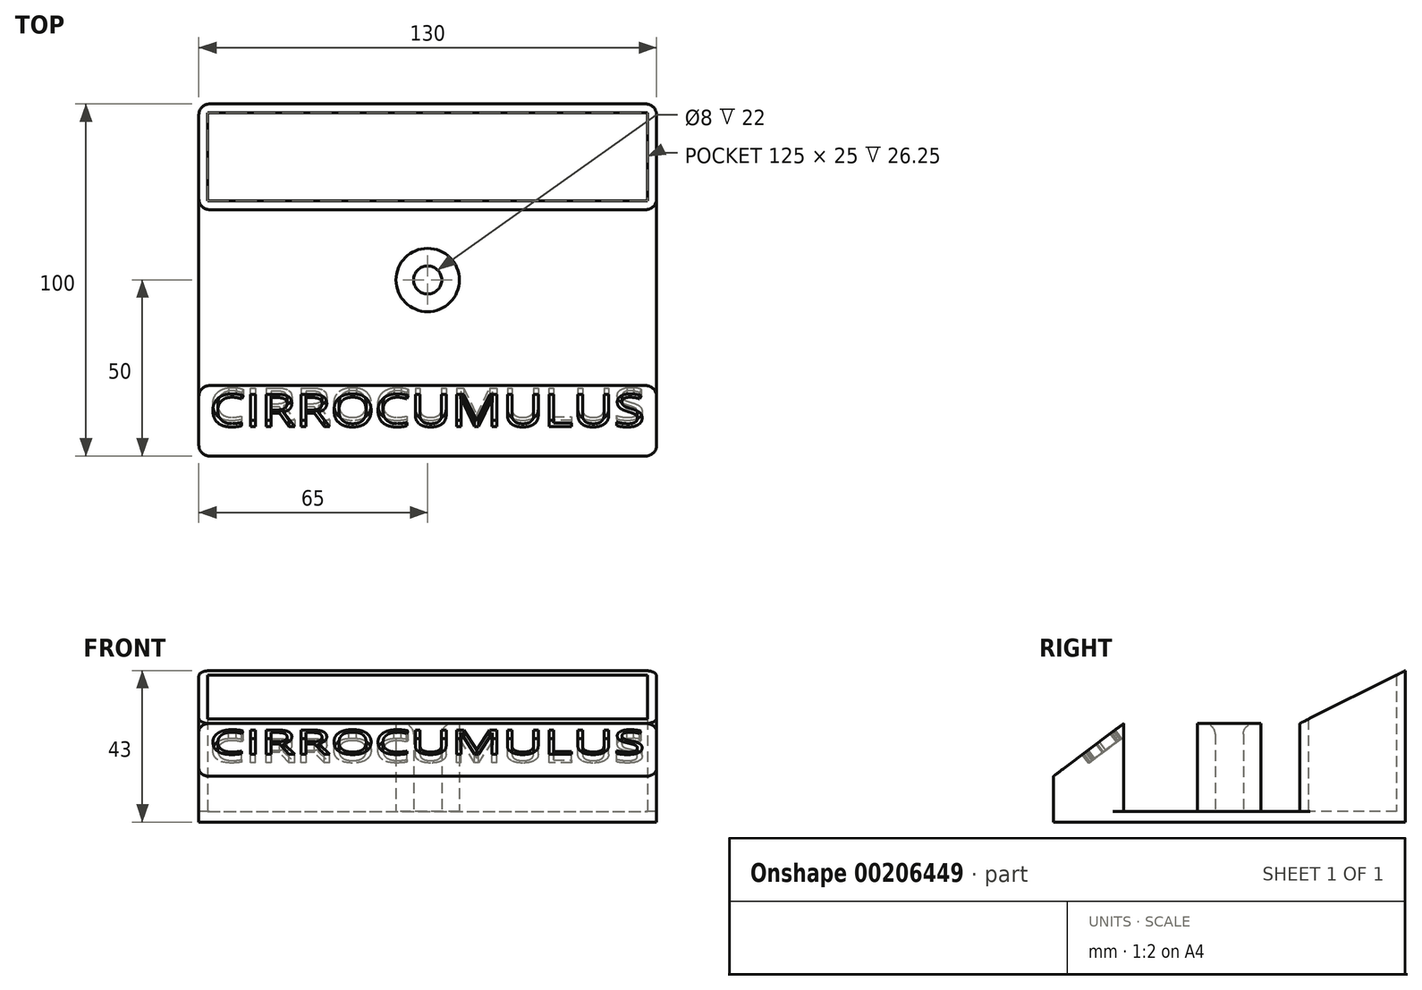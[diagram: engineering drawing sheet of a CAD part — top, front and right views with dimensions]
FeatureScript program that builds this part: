
annotation { "Feature Type Name" : "Feature", "Feature Type Description" : "" }
export const myFeature = defineFeature(function(context is Context, id is Id, definition is map)
    precondition{}
    {
        {
            var Q0;
            Q0=qCreatedBy(makeId("Top.planeOp"),FACE);
            var sketch = newSketch(context, id + "F0", { "sketchPlane" : qUnion([Q0])});
            skLineSegment(sketch, "E0.bottom", {"start": v(-65, 100) * mm, "end": v(65, 100) * mm});
            skLineSegment(sketch, "E0.top", {"start": v(-65, 0) * mm, "end": v(65, 0) * mm});
            skLineSegment(sketch, "E0.left", {"start": v(65, 100) * mm, "end": v(65, 0) * mm});
            skLineSegment(sketch, "E0.right", {"start": v(-65, 100) * mm, "end": v(-65, 0) * mm});
            skSolve(sketch);
        }
        {
            var Q0;
            Q0=makeQuery(id+"F0.imprint","IMPRINT",FACE,{"disambiguationData":[TD([[makeQuery(id+"F0.imprint","IMPRINT",EDGE,{"derivedFrom":sQuery(id+"F0.wireOp",EDGE,"E0.bottom")}),-1.0]])]});
            extrude(context, id + "F1", {"entities" : qUnion([Q0]), "depth" : 3 * mm});
        }
        {
            var Q0;
            Q0=makeQuery(id+"F1.opExtrude","CAP_FACE",FACE,{"disambiguationData":[OSD([sQuery(id+"F0.wireOp",EDGE,"E0.bottom"),sQuery(id+"F0.wireOp",EDGE,"E0.top"),sQuery(id+"F0.wireOp",EDGE,"E0.left"),sQuery(id+"F0.wireOp",EDGE,"E0.right")])],"isStart":false});
            var sketch = newSketch(context, id + "F2", { "sketchPlane" : qUnion([Q0])});
            skLineSegment(sketch, "E1", {"start": v(0, 0) * mm, "end": v(0, 100) * mm, "construction": true});
            skCircle(sketch, "E2", {"center": v(0, 50) * mm, "radius": 9 * mm});
            skCircle(sketch, "E3", {"center": v(0, 50) * mm, "radius": 4 * mm});
            skLineSegment(sketch, "E4.bottom", {"start": v(-65, 0) * mm, "end": v(65, 0) * mm});
            skLineSegment(sketch, "E4.top", {"start": v(-65, 20) * mm, "end": v(65, 20) * mm});
            skLineSegment(sketch, "E4.left", {"start": v(-65, 0) * mm, "end": v(-65, 20) * mm});
            skLineSegment(sketch, "E4.right", {"start": v(65, 0) * mm, "end": v(65, 20) * mm});
            skLineSegment(sketch, "E5.bottom", {"start": v(-65, 100) * mm, "end": v(65, 100) * mm});
            skLineSegment(sketch, "E5.top", {"start": v(-65, 70) * mm, "end": v(65, 70) * mm});
            skLineSegment(sketch, "E5.left", {"start": v(-65, 100) * mm, "end": v(-65, 70) * mm});
            skLineSegment(sketch, "E5.right", {"start": v(65, 100) * mm, "end": v(65, 70) * mm});
            skLineSegment(sketch, "E6.0", {"start": v(62.5, 97.5) * mm, "end": v(62.5, 72.5) * mm});
            skLineSegment(sketch, "E6.1", {"start": v(-62.5, 97.5) * mm, "end": v(62.5, 97.5) * mm});
            skLineSegment(sketch, "E6.2", {"start": v(-62.5, 97.5) * mm, "end": v(-62.5, 72.5) * mm});
            skLineSegment(sketch, "E6.3", {"start": v(-62.5, 72.5) * mm, "end": v(62.5, 72.5) * mm});
            skSolve(sketch);
        }
        {
            var Q0;
            Q0=makeQuery(id+"F2.imprint","IMPRINT",FACE,{"disambiguationData":[TD([[makeQuery(id+"F2.imprint","IMPRINT",EDGE,{"derivedFrom":sQuery(id+"F2.wireOp",EDGE,"E5.bottom")}),-1.0]])]});
            extrude(context, id + "F3", {"entities" : qUnion([Q0]), "operationType" : NewBodyOperationType.ADD, "depth" : 40 * mm});
        }
        {
            var Q0;
            Q0=makeQuery(id+"F2.imprint","IMPRINT",FACE,{"disambiguationData":[TD([[makeQuery(id+"F2.imprint","IMPRINT",EDGE,{"derivedFrom":sQuery(id+"F2.wireOp",EDGE,"E2")}),1.0]])]});
            var Q1;
            Q1=makeQuery(id+"F2.imprint","IMPRINT",FACE,{"disambiguationData":[TD([[makeQuery(id+"F2.imprint","IMPRINT",EDGE,{"derivedFrom":sQuery(id+"F2.wireOp",EDGE,"E4.bottom")}),1.0]])]});
            extrude(context, id + "F4", {"entities" : qUnion([Q0, Q1]), "operationType" : NewBodyOperationType.ADD, "depth" : 25 * mm});
        }
        {
            var Q0;
            Q0=makeQuery(id+"F4.opExtrude","CAP_EDGE",EDGE,{"disambiguationData":[OSD([sQuery(id+"F2.wireOp",EDGE,"E4.bottom")])],"isStart":false});
            chamfer(context, id + "F5", {"entities" : qUnion([Q0]), "chamferType" : ChamferType.TWO_OFFSETS, "width1" : 20 * mm, "oppositeDirection" : false, "width2" : 15 * mm, "tangentPropagation" : true});
        }
        {
            var Q0;
            Q0=makeQuery(id+"F3.opExtrude","CAP_EDGE",EDGE,{"disambiguationData":[OSD([sQuery(id+"F2.wireOp",EDGE,"E5.top")])],"isStart":false});
            chamfer(context, id + "F6", {"entities" : qUnion([Q0]), "chamferType" : ChamferType.TWO_OFFSETS, "width1" : 30 * mm, "oppositeDirection" : false, "width2" : 15 * mm, "tangentPropagation" : true});
        }
        {
            var Q0;
            Q0=makeQuery(id+"F3.boolean.opBoolean","MERGE",EDGE,{"derivedFrom":[makeQuery(id+"F1.opExtrude","SWEPT_EDGE",EDGE,{"disambiguationData":[OSD([sQuery(id+"F0.wireOp",EDGE,"E0.bottom"),sQuery(id+"F0.wireOp",EDGE,"E0.right")])]}),makeQuery(id+"F3.opExtrude","SWEPT_EDGE",EDGE,{"disambiguationData":[OSD([sQuery(id+"F2.wireOp",EDGE,"E5.bottom"),sQuery(id+"F2.wireOp",EDGE,"E5.left")])]})]});
            var Q1;
            Q1=makeQuery(id+"F3.opExtrude","SWEPT_EDGE",EDGE,{"disambiguationData":[OSD([sQuery(id+"F0.wireOp",EDGE,"E0.right"),sQuery(id+"F2.wireOp",EDGE,"E5.top"),sQuery(id+"F2.wireOp",EDGE,"E5.left")])]});
            var Q2;
            Q2=makeQuery(id+"F3.opExtrude","SWEPT_EDGE",EDGE,{"disambiguationData":[OSD([sQuery(id+"F0.wireOp",EDGE,"E0.left"),sQuery(id+"F2.wireOp",EDGE,"E5.top"),sQuery(id+"F2.wireOp",EDGE,"E5.right")])]});
            var Q3;
            Q3=makeQuery(id+"F4.boolean.opBoolean","MERGE",EDGE,{"derivedFrom":[makeQuery(id+"F1.opExtrude","SWEPT_EDGE",EDGE,{"disambiguationData":[OSD([sQuery(id+"F0.wireOp",EDGE,"E0.top"),sQuery(id+"F0.wireOp",EDGE,"E0.right")])]}),makeQuery(id+"F4.opExtrude","SWEPT_EDGE",EDGE,{"disambiguationData":[OSD([sQuery(id+"F2.wireOp",EDGE,"E4.bottom"),sQuery(id+"F2.wireOp",EDGE,"E4.left")])]})]});
            var Q4;
            Q4=makeQuery(id+"F3.boolean.opBoolean","MERGE",EDGE,{"derivedFrom":[makeQuery(id+"F1.opExtrude","SWEPT_EDGE",EDGE,{"disambiguationData":[OSD([sQuery(id+"F0.wireOp",EDGE,"E0.bottom"),sQuery(id+"F0.wireOp",EDGE,"E0.left")])]}),makeQuery(id+"F3.opExtrude","SWEPT_EDGE",EDGE,{"disambiguationData":[OSD([sQuery(id+"F2.wireOp",EDGE,"E5.bottom"),sQuery(id+"F2.wireOp",EDGE,"E5.right")])]})]});
            var Q5;
            Q5=makeQuery(id+"F4.boolean.opBoolean","MERGE",EDGE,{"derivedFrom":[makeQuery(id+"F1.opExtrude","SWEPT_EDGE",EDGE,{"disambiguationData":[OSD([sQuery(id+"F0.wireOp",EDGE,"E0.top"),sQuery(id+"F0.wireOp",EDGE,"E0.left")])]}),makeQuery(id+"F4.opExtrude","SWEPT_EDGE",EDGE,{"disambiguationData":[OSD([sQuery(id+"F2.wireOp",EDGE,"E4.bottom"),sQuery(id+"F2.wireOp",EDGE,"E4.right")])]})]});
            var Q6;
            Q6=makeQuery(id+"F4.opExtrude","SWEPT_EDGE",EDGE,{"disambiguationData":[OSD([sQuery(id+"F0.wireOp",EDGE,"E0.left"),sQuery(id+"F2.wireOp",EDGE,"E4.top"),sQuery(id+"F2.wireOp",EDGE,"E4.right")])]});
            var Q7;
            Q7=makeQuery(id+"F4.opExtrude","SWEPT_EDGE",EDGE,{"disambiguationData":[OSD([sQuery(id+"F0.wireOp",EDGE,"E0.right"),sQuery(id+"F2.wireOp",EDGE,"E4.top"),sQuery(id+"F2.wireOp",EDGE,"E4.left")])]});
            var Q8;
            Q8=makeQuery(id+"F4.opExtrude","CAP_EDGE",EDGE,{"disambiguationData":[OSD([sQuery(id+"F2.wireOp",EDGE,"E3")])],"isStart":false});
            fillet(context, id + "F7", {"entities" : qUnion([Q0, Q1, Q2, Q3, Q4, Q5, Q6, Q7, Q8]), "radius" : 3 * mm, "tangentPropagation" : true, "allowEdgeOverflow" : false});
        }
        {
            var Q0;
            Q0=makeQuery(id+"F5.opChamfer","BLEND_FACE",FACE,{"disambiguationData":[OSD([sQuery(id+"F2.wireOp",EDGE,"E4.bottom")])]});
            var sketch = newSketch(context, id + "F8", { "sketchPlane" : qUnion([Q0])});
            skLineSegment(sketch, "E7.0", {"start": v(62, 10.8) * mm, "end": v(-62, 10.8) * mm});
            skLineSegment(sketch, "E8.0", {"start": v(-62, 29.8) * mm, "end": v(62, 29.8) * mm});
            skText(sketch, "E9", { "text": "CIRROCUMULUS", "fontName": "OpenSans-Regular.ttf"});
            skLineSegment(sketch, "E10", {"start": v(-62, 10.8) * mm, "end": v(-62, 47.82) * mm});
            skLineSegment(sketch, "E11", {"start": v(62, 10.8) * mm, "end": v(62, 49.07) * mm});
            skPoint(sketch, "E11.endSnap0", {"position": v(62, 15.3) * mm});
            const initialGuessF8  = {"E9": [-0.062, 0.01825, 1, 0, 0.01155]};
            skSetInitialGuess(sketch, initialGuessF8);
            skSolve(sketch);
        }
        {
            var Q0;
            Q0=makeQuery(id+"F8.imprint","IMPRINT",FACE,{"disambiguationData":[TD([[makeQuery(id+"F8.imprint","IMPRINT",EDGE,{"derivedFrom":sQuery(id+"F8.wireOp",EDGE,"E9.sketch_text.stroke-0")}),-1.0]])]});
            var Q1;
            Q1=makeQuery(id+"F8.imprint","IMPRINT",FACE,{"disambiguationData":[TD([[makeQuery(id+"F8.imprint","IMPRINT",EDGE,{"derivedFrom":sQuery(id+"F8.wireOp",EDGE,"E9.sketch_text.stroke-13")}),-1.0]])]});
            var Q2;
            Q2=makeQuery(id+"F8.imprint","IMPRINT",FACE,{"disambiguationData":[TD([[makeQuery(id+"F8.imprint","IMPRINT",EDGE,{"derivedFrom":sQuery(id+"F8.wireOp",EDGE,"E9.sketch_text.stroke-19")}),-1.0]])]});
            var Q3;
            Q3=makeQuery(id+"F8.imprint","IMPRINT",FACE,{"disambiguationData":[TD([[makeQuery(id+"F8.imprint","IMPRINT",EDGE,{"derivedFrom":sQuery(id+"F8.wireOp",EDGE,"E9.sketch_text.stroke-27")}),-1.0]])]});
            var Q4;
            Q4=makeQuery(id+"F8.imprint","IMPRINT",FACE,{"disambiguationData":[TD([[makeQuery(id+"F8.imprint","IMPRINT",EDGE,{"derivedFrom":sQuery(id+"F8.wireOp",EDGE,"E9.sketch_text.stroke-43")}),-1.0]])]});
            var Q5;
            Q5=makeQuery(id+"F8.imprint","IMPRINT",FACE,{"disambiguationData":[TD([[makeQuery(id+"F8.imprint","IMPRINT",EDGE,{"derivedFrom":sQuery(id+"F8.wireOp",EDGE,"E9.sketch_text.stroke-58")}),-1.0]])]});
            var Q6;
            Q6=makeQuery(id+"F8.imprint","IMPRINT",FACE,{"disambiguationData":[TD([[makeQuery(id+"F8.imprint","IMPRINT",EDGE,{"derivedFrom":sQuery(id+"F8.wireOp",EDGE,"E9.sketch_text.stroke-72")}),-1.0]])]});
            var Q7;
            Q7=makeQuery(id+"F8.imprint","IMPRINT",FACE,{"disambiguationData":[TD([[makeQuery(id+"F8.imprint","IMPRINT",EDGE,{"derivedFrom":sQuery(id+"F8.wireOp",EDGE,"E9.sketch_text.stroke-90")}),-1.0]])]});
            var Q8;
            Q8=makeQuery(id+"F8.imprint","IMPRINT",FACE,{"disambiguationData":[TD([[makeQuery(id+"F8.imprint","IMPRINT",EDGE,{"derivedFrom":sQuery(id+"F8.wireOp",EDGE,"E9.sketch_text.stroke-104")}),-1.0]])]});
            var Q9;
            Q9=makeQuery(id+"F8.imprint","IMPRINT",FACE,{"disambiguationData":[TD([[makeQuery(id+"F8.imprint","IMPRINT",EDGE,{"derivedFrom":sQuery(id+"F8.wireOp",EDGE,"E9.sketch_text.stroke-110")}),-1.0]])]});
            var Q10;
            Q10=makeQuery(id+"F8.imprint","IMPRINT",FACE,{"disambiguationData":[TD([[makeQuery(id+"F8.imprint","IMPRINT",EDGE,{"derivedFrom":sQuery(id+"F8.wireOp",EDGE,"E9.sketch_text.stroke-124")}),-1.0]])]});
            var Q11;
            Q11=makeQuery(id+"F8.imprint","IMPRINT",FACE,{"disambiguationData":[TD([[makeQuery(id+"F8.imprint","IMPRINT",EDGE,{"derivedFrom":sQuery(id+"F8.wireOp",EDGE,"E9.sketch_text.stroke-15")}),-1.0]])]});
            var Q12;
            Q12=makeQuery(id+"F8.imprint","IMPRINT",FACE,{"disambiguationData":[TD([[makeQuery(id+"F8.imprint","IMPRINT",EDGE,{"derivedFrom":sQuery(id+"F8.wireOp",EDGE,"E9.sketch_text.stroke-132")}),-1.0]])]});
            var Q13;
            Q13=makeQuery(id+"F8.imprint","IMPRINT",FACE,{"disambiguationData":[TD([[makeQuery(id+"F8.imprint","IMPRINT",EDGE,{"derivedFrom":sQuery(id+"F8.wireOp",EDGE,"E9.sketch_text.stroke-138")}),-1.0]])]});
            var Q14;
            Q14=makeQuery(id+"F8.imprint","IMPRINT",FACE,{"disambiguationData":[TD([[makeQuery(id+"F8.imprint","IMPRINT",EDGE,{"derivedFrom":sQuery(id+"F8.wireOp",EDGE,"E9.sketch_text.stroke-152")}),-1.0]])]});
            extrude(context, id + "F9", {"entities" : qUnion([Q0, Q1, Q2, Q3, Q4, Q5, Q6, Q7, Q8, Q9, Q10, Q11, Q12, Q13, Q14]), "operationType" : NewBodyOperationType.REMOVE, "oppositeDirection" : true, "depth" : 3 * mm});
        }
    });
